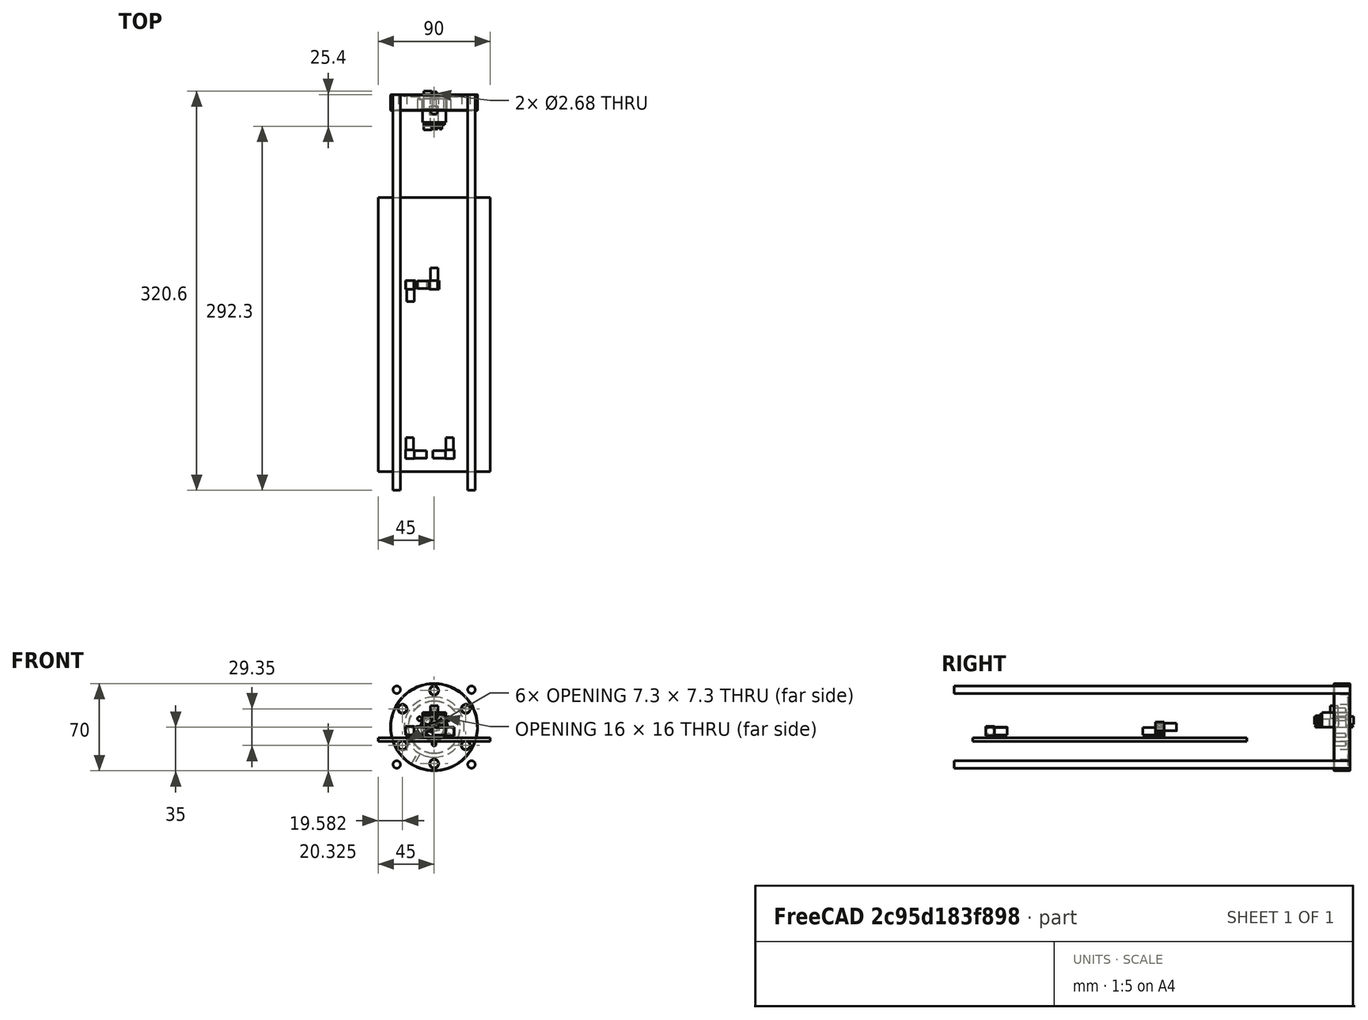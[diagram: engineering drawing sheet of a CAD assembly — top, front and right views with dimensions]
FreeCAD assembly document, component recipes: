
FREECAD ASSEMBLY — COMPONENT RECIPES ("MechanicalCF35Mount_Assembly")

This assembly document has 11 components, labeled P0..P10 below (a component is one placed body or linked part). 6 of them carry a construction recipe — the FreeCAD feature program that regenerates the part from scratch, quoted from this document or its linked companion documents; the rest are supplied as boundary geometry only. No exploded tour is included for this assembly.
COMPONENT P0 — recipe-attached ("Frontplane", a linked part whose construction recipe lives in a companion FreeCAD document of the same project; that document's serialized recipe follows).
Construction recipe (the companion document, serialized — sketch geometry with constraints, then the solid features built on it; lengths are millimeters unless a unit is written):

FCSTD DOCUMENT  (FreeCAD 0.20R29603 (Git))
Label: MechanicalCF35Mount001
License: All rights reserved
LicenseURL: http://en.wikipedia.org/wiki/All_rights_reserved
objects: Part::Feature×20, Part::Cylinder×15, TechDraw::DrawViewDimension×13, Part::Compound×12, TechDraw::DrawProjGroupItem×5, Part::Cut×4, Part::Box×1, Part::Fillet×1, TechDraw::DrawSVGTemplate×1, TechDraw::DrawProjGroup×1, TechDraw::DrawPage×1
note: 53 computed .brp shape members not serialized (recipe doc carries the construction recipe); baked Part::Feature solids carry a one-line shape summary decoded from their .brp

FEATURE [Part::Feature] Solid  label="Hositrad_CFA35-16D"
  shape: bbox 70 x 12.7 x 70 mm, 88 faces (baked)
FEATURE [Part::Feature] _7192_01_CF
  shape: bbox 33.78 x 40.23 x 14.22 mm, 39 faces, 0 solids (baked)
FEATURE [Part::Feature] _7192_01_CF001
  Placement = pos=(0,0,-39.0113) rot=(1,0,0;1.5708rad)
  shape: bbox 14 x 7.506 x 26.34 mm, 46 faces, 0 solids (baked)
FEATURE [Part::Feature] _7192_01_CF002
  Placement = pos=(0,0,-58.2625) rot=(-0.03621,0.706643,0.706643;3.21398rad)
  shape: bbox 18.12 x 10.39 x 7.838 mm, 29 faces, 0 solids (baked)
FEATURE [Part::Feature] _7192_01_CF003
  Placement = pos=(0,0,-42.2965) rot=(0.8891,-0.323652,-0.323652;1.68807rad)
  shape: bbox 16.99 x 16.03 x 5.603 mm, 25 faces, 0 solids (baked)
FEATURE [Part::Feature] _7192_01_CF004
  Placement = pos=(0,0,-35.56) rot=(0,0.707107,-0.707107;3.14159rad)
  shape: bbox 22.78 x 12.72 x 33.85 mm, 35 faces, 0 solids (baked)
FEATURE [Part::Feature] _7192_01_CF005
  Placement = pos=(0,0,-36.7339) rot=(0.997746,-0.047454,-0.047454;1.57305rad)
  shape: bbox 7.007 x 7.007 x 0.8128 mm, 6 faces, 0 solids (baked)
FEATURE [Part::Feature] _7192_01_CF006
  Placement = pos=(0,0,-66.0654) rot=(0.57735,0.57735,0.57735;2.0944rad)
  shape: bbox 2.416 x 2.416 x 39.37 mm, 29 faces, 0 solids (baked)
FEATURE [Part::Feature] _7192_01_CF007
  Placement = pos=(0,0,-32.2253) rot=(0.196732,0.693288,-0.693288;3.5301rad)
  shape: bbox 26.96 x 26.96 x 13.28 mm, 55 faces, 0 solids (baked)
FEATURE [Part::Feature] _7192_01_CF008
  Placement = pos=(0,0,-46.1699) rot=(0.196732,0.693288,-0.693288;3.5301rad)
  shape: bbox 34.28 x 29.27 x 4.775 mm, 16 faces, 0 solids (baked)
FEATURE [Part::Feature] _7192_01_CF009
  Placement = pos=(0,0,-22.86) rot=(0.196732,0.693288,-0.693288;3.5301rad)
  shape: bbox 24.3 x 24.3 x 12.6 mm, 19 faces, 0 solids (baked)
FEATURE [Part::Feature] _7192_01_CF010
  Placement = pos=(0,0,-12.7) rot=(0.196732,0.693288,-0.693288;3.5301rad)
  shape: bbox 26.42 x 26.42 x 12.7 mm, 14 faces, 0 solids (baked)
FEATURE [Part::Feature] _7192_01_CF011
  Placement = pos=(0,0,-42.1821) rot=(0.196732,0.693288,-0.693288;3.5301rad)
  shape: bbox 43.95 x 37.52 x 5.044 mm, 27 faces, 0 solids (baked)
FEATURE [Part::Feature] _7192_01_CF012
  Placement = pos=(0,0,-35.56) rot=(0.079728,0.704856,0.704856;2.98247rad)
  shape: bbox 15.4 x 15.4 x 39.12 mm, 6 faces, 0 solids (baked)
FEATURE [Part::Feature] _7192_01_CF013
  Placement = pos=(0,0,-26.6954) rot=(0.165786,0.697322,0.697322;2.81301rad)
  shape: bbox 5.339 x 4.281 x 34.06 mm, 6 faces, 0 solids (baked)
FEATURE [Part::Feature] _7192_01_CF014
  Placement = pos=(0,0,6.7564) rot=(0.205998,0.691941,-0.691941;3.54791rad)
  shape: bbox 9.907 x 7.446 x 1.311 mm, 4 faces, 0 solids (baked)
FEATURE [Part::Feature] _7192_01_CF015
  Placement = pos=(0,0,-7.9756) rot=(1,0,0;1.5708rad)
  shape: bbox 22.78 x 12.72 x 22.32 mm, 35 faces, 0 solids (baked)
FEATURE [Part::Feature] _7192_01_CF016
  Placement = pos=(0,0,22.3805) rot=(0.205998,0.691941,-0.691941;3.54791rad)
  shape: bbox 3.344 x 3.344 x 15.27 mm, 29 faces, 0 solids (baked)
FEATURE [Part::Feature] _7192_01_CF017
  Placement = pos=(0,0,6.7564) rot=(1,0,0;1.5708rad)
  shape: bbox 10.8 x 10.8 x 1.524 mm, 10 faces, 0 solids (baked)
FEATURE [Part::Compound] Compound  label="CF16BNCFeedthrough"
  Links = -> [_7192_01_CF,_7192_01_CF001,_7192_01_CF002,_7192_01_CF003,_7192_01_CF004,_7192_01_CF005,_7192_01_CF006,_7192_01_CF007,_7192_01_CF008,_7192_01_CF009,_7192_01_CF010,_7192_01_CF011,_7192_01_CF012,_7192_01_CF013,_7192_01_CF014,_7192_01_CF015,_7192_01_CF016,_7192_01_CF017]
  Placement = pos=(0,0,0) rot=(-1,0,0;1.5708rad)
FEATURE [Part::Box] Box  label="Würfel"
  AttacherType = Attacher::AttachEngine3D
  Height = 100
  Length = 100
  Placement = pos=(-50,0,-50) rot=(0,0,1;0rad)
  Width = 12.7
FEATURE [Part::Cylinder] Cylinder  label="Zylinder"
  Angle = 360
  AttacherType = Attacher::AttachEngine3D
  FirstAngle = 0
  Height = 12.7
  Placement = pos=(0,12.7,0) rot=(1,0,0;1.5708rad)
  Radius = 35.5
  SecondAngle = 0
FEATURE [Part::Cut] Cut
  Base = -> Box
  Tool = -> Cylinder
FEATURE [Part::Cylinder] Cylinder001  label="Zylinder001"
  Angle = 360
  AttacherType = Attacher::AttachEngine3D
  FirstAngle = 0
  Height = 100
  Placement = pos=(0,6.35,-50) rot=(0,0,1;0rad)
  Radius = 2.46
  SecondAngle = 0
FEATURE [Part::Cylinder] Cylinder002  label="Zylinder002"
  Angle = 360
  AttacherType = Attacher::AttachEngine3D
  FirstAngle = 0
  Height = 100
  Placement = pos=(0,6.35,-50) rot=(0,0,1;0rad)
  Radius = 2.46
  SecondAngle = 0
FEATURE [Part::Compound] Compound001
  Links = -> [Cylinder002]
  Placement = pos=(0,0,0) rot=(0,1,0;1.5708rad)
FEATURE [Part::Compound] Compound002  label="SetscrewCoreholes"
  Links = -> [Compound001,Cylinder001]
FEATURE [Part::Cut] Cut001
  Base = -> Cut
  Tool = -> Compound002
FEATURE [Part::Cylinder] Cylinder003  label="Zylinder003"
  Angle = 360
  AttacherType = Attacher::AttachEngine3D
  FirstAngle = 0
  Height = 12
  Placement = pos=(-30,6.3,-50) rot=(0,0,1;0rad)
  Radius = 2.46
  SecondAngle = 0
FEATURE [Part::Cylinder] Cylinder004  label="Zylinder004"
  Angle = 360
  AttacherType = Attacher::AttachEngine3D
  FirstAngle = 0
  Height = 12
  Placement = pos=(30,6.3,-50) rot=(0,0,1;0rad)
  Radius = 2.46
  SecondAngle = 0
FEATURE [Part::Compound] Compound003
  Links = -> [Cylinder003,Cylinder004]
FEATURE [Part::Cylinder] Cylinder005  label="Zylinder005"
  Angle = 360
  AttacherType = Attacher::AttachEngine3D
  FirstAngle = 0
  Height = 12
  Placement = pos=(-30,6.3,-50) rot=(0,0,1;0rad)
  Radius = 2.46
  SecondAngle = 0
FEATURE [Part::Cylinder] Cylinder006  label="Zylinder006"
  Angle = 360
  AttacherType = Attacher::AttachEngine3D
  FirstAngle = 0
  Height = 12
  Placement = pos=(30,6.3,-50) rot=(0,0,1;0rad)
  Radius = 2.46
  SecondAngle = 0
FEATURE [Part::Compound] Compound004
  Links = -> [Cylinder005,Cylinder006]
  Placement = pos=(0,0,0) rot=(0,-1,0;1.5708rad)
FEATURE [Part::Cylinder] Cylinder007  label="Zylinder007"
  Angle = 360
  AttacherType = Attacher::AttachEngine3D
  FirstAngle = 0
  Height = 12
  Placement = pos=(-30,6.3,-50) rot=(0,0,1;0rad)
  Radius = 2.46
  SecondAngle = 0
FEATURE [Part::Cylinder] Cylinder008  label="Zylinder008"
  Angle = 360
  AttacherType = Attacher::AttachEngine3D
  FirstAngle = 0
  Height = 12
  Placement = pos=(30,6.3,-50) rot=(0,0,1;0rad)
  Radius = 2.46
  SecondAngle = 0
FEATURE [Part::Compound] Compound005
  Links = -> [Cylinder007,Cylinder008]
  Placement = pos=(0,0,0) rot=(0,1,0;3.14159rad)
FEATURE [Part::Cylinder] Cylinder009  label="Zylinder009"
  Angle = 360
  AttacherType = Attacher::AttachEngine3D
  FirstAngle = 0
  Height = 12
  Placement = pos=(-30,6.3,-50) rot=(0,0,1;0rad)
  Radius = 2.46
  SecondAngle = 0
FEATURE [Part::Cylinder] Cylinder010  label="Zylinder010"
  Angle = 360
  AttacherType = Attacher::AttachEngine3D
  FirstAngle = 0
  Height = 12
  Placement = pos=(30,6.3,-50) rot=(0,0,1;0rad)
  Radius = 2.46
  SecondAngle = 0
FEATURE [Part::Compound] Compound006
  Links = -> [Cylinder009,Cylinder010]
  Placement = pos=(0,0,0) rot=(0,1,0;-4.71239rad)
FEATURE [Part::Compound] Compound007  label="M6Mountscrews"
  Links = -> [Compound003,Compound004,Compound005,Compound006]
FEATURE [Part::Cut] Cut002
  Base = -> Cut001
  Tool = -> Compound007
FEATURE [Part::Cylinder] Cylinder011  label="Zylinder011"
  Angle = 360
  AttacherType = Attacher::AttachEngine3D
  FirstAngle = 0
  Height = 300
  Placement = pos=(30,12.7,30) rot=(1,0,0;1.5708rad)
  Radius = 2.38
  SecondAngle = 0
FEATURE [Part::Cylinder] Cylinder012  label="Zylinder012"
  Angle = 360
  AttacherType = Attacher::AttachEngine3D
  FirstAngle = 0
  Height = 300
  Placement = pos=(30,12.7,30) rot=(1,0,0;1.5708rad)
  Radius = 2.38
  SecondAngle = 0
FEATURE [Part::Compound] Compound008
  Links = -> [Cylinder012]
  Placement = pos=(0,0,0) rot=(0,1,0;1.5708rad)
FEATURE [Part::Cylinder] Cylinder013  label="Zylinder013"
  Angle = 360
  AttacherType = Attacher::AttachEngine3D
  FirstAngle = 0
  Height = 300
  Placement = pos=(30,12.7,30) rot=(1,0,0;1.5708rad)
  Radius = 2.38
  SecondAngle = 0
FEATURE [Part::Compound] Compound009
  Links = -> [Cylinder013]
  Placement = pos=(0,0,0) rot=(0,1,0;3.14159rad)
FEATURE [Part::Cylinder] Cylinder014  label="Zylinder014"
  Angle = 360
  AttacherType = Attacher::AttachEngine3D
  FirstAngle = 0
  Height = 300
  Placement = pos=(30,12.7,30) rot=(1,0,0;1.5708rad)
  Radius = 2.38
  SecondAngle = 0
FEATURE [Part::Compound] Compound010
  Links = -> [Cylinder014]
  Placement = pos=(0,0,0) rot=(0,-1,0;1.5708rad)
FEATURE [Part::Compound] Compound014  label="M6ThreadRods"
  Links = -> [Cylinder011,Compound008,Compound009,Compound010]
FEATURE [Part::Cut] Cut003
  Base = -> Cut002
  Tool = -> Compound014
FEATURE [Part::Fillet] Fillet
  Base = -> Cut003
  Edges = 2 edges r=2: [Edge2,Edge3]
FEATURE [Part::Feature] Fillet_solid  label="Fillet (Solid)"
  shape: bbox 100 x 12.7 x 100 mm, 33 faces (baked)
FEATURE [TechDraw::DrawSVGTemplate] Template
  EditableTexts = Designed_by_Name=Thomas Spielauer; FC-Date=2023-07-05; FC-SC=mm; FC-SH=01; FC-Title=CF40 electronics housing; Subtitle=Front plate
  Height = 210
  Orientation = 1
  Width = 297
FEATURE [TechDraw::DrawProjGroupItem] ProjItem  label="Front"
  CoarseView = false
  Direction = (0,-1,0)
  Focus = 100
  HardHidden = false
  IsoCount = 0
  IsoHidden = false
  IsoVisible = false
  LockPosition = true
  Perspective = false
  Rotation = 0
  RotationVector = (0,0,1)
  ScaleType = 2
  SeamHidden = false
  SeamVisible = true
  SmoothHidden = false
  SmoothVisible = true
  Source = -> [Fillet]
  Type = 0
  X = 0
  XDirection = (0,0,1)
  Y = 0
FEATURE [TechDraw::DrawProjGroupItem] ProjItem001  label="Right"
  CoarseView = false
  Direction = (0,-1e-16,1)
  Focus = 100
  HardHidden = false
  IsoCount = 0
  IsoHidden = false
  IsoVisible = false
  LockPosition = false
  Perspective = false
  Rotation = 0
  RotationVector = (1,0,0)
  ScaleType = 2
  SeamHidden = false
  SeamVisible = true
  SmoothHidden = false
  SmoothVisible = true
  Source = -> [Fillet]
  Type = 2
  X = -67.6611
  XDirection = (0,1,1e-16)
  Y = 0
FEATURE [TechDraw::DrawProjGroupItem] ProjItem002  label="Bottom"
  CoarseView = false
  Direction = (1,0,0)
  Focus = 100
  HardHidden = false
  IsoCount = 0
  IsoHidden = false
  IsoVisible = false
  LockPosition = false
  Perspective = false
  Rotation = 0
  RotationVector = (1,0,0)
  ScaleType = 2
  SeamHidden = false
  SeamVisible = true
  SmoothHidden = false
  SmoothVisible = true
  Source = -> [Fillet]
  Type = 5
  X = 0
  XDirection = (0,0,1)
  Y = 73.816
FEATURE [TechDraw::DrawProjGroupItem] ProjItem003  label="Left"
  CoarseView = false
  Direction = (0,-1e-16,-1)
  Focus = 100
  HardHidden = false
  IsoCount = 0
  IsoHidden = false
  IsoVisible = false
  LockPosition = false
  Perspective = false
  Rotation = 0
  RotationVector = (1,0,0)
  ScaleType = 2
  SeamHidden = false
  SeamVisible = true
  SmoothHidden = false
  SmoothVisible = true
  Source = -> [Fillet]
  Type = 1
  X = 105.155
  XDirection = (0,-1,1e-16)
  Y = 0
FEATURE [TechDraw::DrawProjGroupItem] ProjItem004  label="Top"
  CoarseView = false
  Direction = (-1,0,0)
  Focus = 100
  HardHidden = false
  IsoCount = 0
  IsoHidden = false
  IsoVisible = false
  LockPosition = false
  Perspective = false
  Rotation = 0
  RotationVector = (1,0,0)
  ScaleType = 2
  SeamHidden = false
  SeamVisible = true
  SmoothHidden = false
  SmoothVisible = true
  Source = -> [Fillet]
  Type = 4
  X = 0
  XDirection = (0,0,1)
  Y = -75.3562
FEATURE [TechDraw::DrawProjGroup] ProjGroup
  Anchor = -> ProjItem
  AutoDistribute = true
  LockPosition = false
  ProjectionType = 0
  Rotation = 0
  ScaleType = 0
  Source = -> [Fillet]
  Views = -> [ProjItem,ProjItem001,ProjItem002,ProjItem003,ProjItem004]
  X = 91.0868
  Y = 118.279
  spacingX = 0
  spacingY = 0
FEATURE [TechDraw::DrawViewDimension] Dimension
  AngleOverride = false
  Arbitrary = false
  ArbitraryTolerances = false
  EqualTolerance = true
  ExtensionAngle = 0
  FormatSpec = %.2w
  FormatSpecOverTolerance = %+.2w
  FormatSpecUnderTolerance = %+.2w
  Inverted = false
  LineAngle = 0
  LockPosition = false
  MeasureType = 1
  OverTolerance = 0
  References2D = -> [ProjItem003]
  Rotation = 0
  ScaleType = 0
  TheoreticalExact = false
  Type = 0
  UnderTolerance = 0
  X = 27.7422
  Y = 2.49993
FEATURE [TechDraw::DrawViewDimension] Dimension001
  AngleOverride = false
  Arbitrary = false
  ArbitraryTolerances = false
  EqualTolerance = true
  ExtensionAngle = 0
  FormatSpec = %.2w
  FormatSpecOverTolerance = %+.2w
  FormatSpecUnderTolerance = %+.2w
  Inverted = false
  LineAngle = 0
  LockPosition = false
  MeasureType = 1
  OverTolerance = 0
  References2D = -> [ProjItem004]
  Rotation = 0
  ScaleType = 0
  TheoreticalExact = false
  Type = 0
  UnderTolerance = 0
  X = -0.515822
  Y = -20.0124
FEATURE [TechDraw::DrawViewDimension] Dimension002
  AngleOverride = false
  Arbitrary = false
  ArbitraryTolerances = false
  EqualTolerance = true
  ExtensionAngle = 0
  FormatSpec = ⌀%.2w
  FormatSpecOverTolerance = %+.2w
  FormatSpecUnderTolerance = %+.2w
  Inverted = false
  LineAngle = 0
  LockPosition = false
  MeasureType = 1
  OverTolerance = 0
  References2D = -> [ProjItem]
  Rotation = 0
  ScaleType = 0
  TheoreticalExact = false
  Type = 5
  UnderTolerance = 0
  X = 0.325472
  Y = 8.03302
FEATURE [TechDraw::DrawViewDimension] Dimension003
  AngleOverride = false
  Arbitrary = false
  ArbitraryTolerances = false
  EqualTolerance = true
  ExtensionAngle = 0
  FormatSpec = ⌀%.2w (M6 4x)
  FormatSpecOverTolerance = %+.2w
  FormatSpecUnderTolerance = %+.2w
  Inverted = false
  LineAngle = 0
  LockPosition = false
  MeasureType = 1
  OverTolerance = 0
  References2D = -> [ProjItem]
  Rotation = 0
  ScaleType = 0
  TheoreticalExact = false
  Type = 5
  UnderTolerance = 0
  X = -23.9583
  Y = 40.0197
FEATURE [TechDraw::DrawViewDimension] Dimension004
  AngleOverride = false
  Arbitrary = false
  ArbitraryTolerances = false
  EqualTolerance = true
  ExtensionAngle = 0
  FormatSpec = %.2w
  FormatSpecOverTolerance = %+.2w
  FormatSpecUnderTolerance = %+.2w
  Inverted = false
  LineAngle = 0
  LockPosition = false
  MeasureType = 1
  OverTolerance = 0
  References2D = -> [ProjItem]
  Rotation = 0
  ScaleType = 0
  TheoreticalExact = false
  Type = 0
  UnderTolerance = 0
  X = 39.4213
  Y = 67.0173
FEATURE [TechDraw::DrawViewDimension] Dimension005
  AngleOverride = false
  Arbitrary = false
  ArbitraryTolerances = false
  EqualTolerance = true
  ExtensionAngle = 0
  FormatSpec = %.2w
  FormatSpecOverTolerance = %+.2w
  FormatSpecUnderTolerance = %+.2w
  Inverted = false
  LineAngle = 0
  LockPosition = false
  MeasureType = 1
  OverTolerance = 0
  References2D = -> [ProjItem]
  Rotation = 0
  ScaleType = 0
  TheoreticalExact = false
  Type = 0
  UnderTolerance = 0
  X = 34.38
  Y = 42.4999
FEATURE [TechDraw::DrawViewDimension] Dimension006
  AngleOverride = false
  Arbitrary = false
  ArbitraryTolerances = false
  EqualTolerance = true
  ExtensionAngle = 0
  FormatSpec = %.2w
  FormatSpecOverTolerance = %+.2w
  FormatSpecUnderTolerance = %+.2w
  Inverted = false
  LineAngle = 0
  LockPosition = false
  MeasureType = 1
  OverTolerance = 0
  References2D = -> [ProjItem]
  Rotation = 0
  ScaleType = 0
  TheoreticalExact = false
  Type = 0
  UnderTolerance = 0
  X = 71.4033
  Y = -19.5166
FEATURE [TechDraw::DrawViewDimension] Dimension007
  AngleOverride = false
  Arbitrary = false
  ArbitraryTolerances = false
  EqualTolerance = true
  ExtensionAngle = 0
  FormatSpec = %.2w
  FormatSpecOverTolerance = %+.2w
  FormatSpecUnderTolerance = %+.2w
  Inverted = false
  LineAngle = 0
  LockPosition = false
  MeasureType = 1
  OverTolerance = 0
  References2D = -> [ProjItem]
  Rotation = 0
  ScaleType = 0
  TheoreticalExact = false
  Type = 0
  UnderTolerance = 0
  X = -1.26969
  Y = 60.8859
FEATURE [TechDraw::DrawViewDimension] Dimension008
  AngleOverride = false
  Arbitrary = false
  ArbitraryTolerances = false
  EqualTolerance = true
  ExtensionAngle = 0
  FormatSpec = ⌀%.2w (M6 3x pro Seite)
  FormatSpecOverTolerance = %+.2w
  FormatSpecUnderTolerance = %+.2w
  Inverted = false
  LineAngle = 0
  LockPosition = false
  MeasureType = 1
  OverTolerance = 0
  References2D = -> [ProjItem003]
  Rotation = 0
  ScaleType = 0
  TheoreticalExact = false
  Type = 5
  UnderTolerance = 0
  X = 55.193
  Y = 36.5443
FEATURE [TechDraw::DrawViewDimension] Dimension009
  AngleOverride = false
  Arbitrary = false
  ArbitraryTolerances = false
  EqualTolerance = true
  ExtensionAngle = 0
  FormatSpec = %.2w
  FormatSpecOverTolerance = %+.2w
  FormatSpecUnderTolerance = %+.2w
  Inverted = false
  LineAngle = 0
  LockPosition = false
  MeasureType = 1
  OverTolerance = 0
  References2D = -> [ProjItem003]
  Rotation = 0
  ScaleType = 0
  TheoreticalExact = false
  Type = 0
  UnderTolerance = 0
  X = -14.0854
  Y = 64.8143
FEATURE [TechDraw::DrawViewDimension] Dimension010
  AngleOverride = false
  Arbitrary = false
  ArbitraryTolerances = false
  EqualTolerance = true
  ExtensionAngle = 0
  FormatSpec = %.2w
  FormatSpecOverTolerance = %+.2w
  FormatSpecUnderTolerance = %+.2w
  Inverted = false
  LineAngle = 0
  LockPosition = false
  MeasureType = 1
  OverTolerance = 0
  References2D = -> [ProjItem003]
  Rotation = 0
  ScaleType = 0
  TheoreticalExact = false
  Type = 0
  UnderTolerance = 0
  X = -20.8153
  Y = 17.1561
FEATURE [TechDraw::DrawViewDimension] Dimension011
  AngleOverride = false
  Arbitrary = false
  ArbitraryTolerances = false
  EqualTolerance = true
  ExtensionAngle = 0
  FormatSpec = %.2w
  FormatSpecOverTolerance = %+.2w
  FormatSpecUnderTolerance = %+.2w
  Inverted = false
  LineAngle = 0
  LockPosition = false
  MeasureType = 1
  OverTolerance = 0
  References2D = -> [ProjItem003]
  Rotation = 0
  ScaleType = 0
  TheoreticalExact = false
  Type = 0
  UnderTolerance = 0
  X = -20.7966
  Y = -12.5001
FEATURE [TechDraw::DrawViewDimension] Dimension012
  AngleOverride = false
  Arbitrary = false
  ArbitraryTolerances = false
  EqualTolerance = true
  ExtensionAngle = 0
  FormatSpec = %.2w
  FormatSpecOverTolerance = %+.2w
  FormatSpecUnderTolerance = %+.2w
  Inverted = false
  LineAngle = 0
  LockPosition = false
  MeasureType = 1
  OverTolerance = 0
  References2D = -> [ProjItem003]
  Rotation = 0
  ScaleType = 0
  TheoreticalExact = false
  Type = 0
  UnderTolerance = 0
  X = 15.28
  Y = -53.2031
FEATURE [TechDraw::DrawPage] Page
  KeepUpdated = true
  NextBalloonIndex = 1
  ProjectionType = 0
  Template = -> Template
  Views = -> [ProjGroup,Dimension,Dimension001,Dimension002,Dimension003,Dimension004,Dimension005,Dimension006,Dimension007,Dimension008,Dimension009,Dimension010,Dimension011,Dimension012]
COMPONENT P1 — geometry summary ("Backplane"; no construction recipe available for this part):
  bounding box: 100.0 x 100.0 x 4.0 mm
  tessellated surface: 3,356 triangles
  volume: 39570 mm^3 (99% of its bounding box)
  symmetry: 2-fold rotationally symmetric about the y axis; 2-fold rotationally symmetric about the z axis; mirror-symmetric across its x mid-plane, z mid-plane
COMPONENT P2 — geometry summary ("Coversheet"; no construction recipe available for this part):
  bounding box: 317.7 x 105.4 x 103.6 mm
  tessellated surface: 6,192 triangles
  volume: 177131 mm^3 (5% of its bounding box)
  symmetry: 2-fold rotationally symmetric about the z axis; mirror-symmetric across its x mid-plane, y mid-plane
COMPONENT P3 — recipe-attached ("Bottomplane", a linked part whose construction recipe lives in a companion FreeCAD document of the same project; that document's serialized recipe follows).
Construction recipe (the companion document, serialized — sketch geometry with constraints, then the solid features built on it; lengths are millimeters unless a unit is written):

FCSTD DOCUMENT  (FreeCAD 0.20R29603 (Git))
Label: MechanicalCF35Mount004
License: All rights reserved
LicenseURL: http://en.wikipedia.org/wiki/All_rights_reserved
objects: Part::Cylinder×14, Part::Compound×10, TechDraw::DrawViewDimension×8, TechDraw::DrawProjGroupItem×2, Part::Box×1, Part::Cut×1, Part::Feature×1, TechDraw::DrawSVGTemplate×1, TechDraw::DrawProjGroup×1, TechDraw::DrawPage×1
note: 27 computed .brp shape members not serialized (recipe doc carries the construction recipe); baked Part::Feature solids carry a one-line shape summary decoded from their .brp

FEATURE [Part::Box] Box  label="Würfel"
  AttacherType = Attacher::AttachEngine3D
  Height = 1.8
  Length = 100
  Placement = pos=(-50,-305,50) rot=(0,0,1;0rad)
  Width = 317.7
FEATURE [Part::Cylinder] Cylinder  label="Zylinder"
  Angle = 360
  AttacherType = Attacher::AttachEngine3D
  FirstAngle = 0
  Height = 20
  Placement = pos=(30,2,40) rot=(0,0,1;0rad)
  Radius = 1.2
  SecondAngle = 0
FEATURE [Part::Cylinder] Cylinder015  label="Zylinder015"
  Angle = 360
  AttacherType = Attacher::AttachEngine3D
  FirstAngle = 0
  Height = 20
  Placement = pos=(-30,2,40) rot=(0,0,1;0rad)
  Radius = 1.2
  SecondAngle = 0
FEATURE [Part::Compound] Compound
  Links = -> [Cylinder,Cylinder015]
FEATURE [Part::Cylinder] Cylinder016  label="Zylinder016"
  Angle = 360
  AttacherType = Attacher::AttachEngine3D
  FirstAngle = 0
  Height = 20
  Placement = pos=(30,2,40) rot=(0,0,1;0rad)
  Radius = 1.2
  SecondAngle = 0
FEATURE [Part::Cylinder] Cylinder017  label="Zylinder017"
  Angle = 360
  AttacherType = Attacher::AttachEngine3D
  FirstAngle = 0
  Height = 20
  Placement = pos=(-30,2,40) rot=(0,0,1;0rad)
  Radius = 1.2
  SecondAngle = 0
FEATURE [Part::Compound] Compound015
  Links = -> [Cylinder016,Cylinder017]
  Placement = pos=(0,0,0) rot=(0,1,0;1.5708rad)
FEATURE [Part::Cylinder] Cylinder018  label="Zylinder018"
  Angle = 360
  AttacherType = Attacher::AttachEngine3D
  FirstAngle = 0
  Height = 20
  Placement = pos=(30,2,40) rot=(0,0,1;0rad)
  Radius = 1.2
  SecondAngle = 0
FEATURE [Part::Cylinder] Cylinder019  label="Zylinder019"
  Angle = 360
  AttacherType = Attacher::AttachEngine3D
  FirstAngle = 0
  Height = 20
  Placement = pos=(-30,2,40) rot=(0,0,1;0rad)
  Radius = 1.2
  SecondAngle = 0
FEATURE [Part::Compound] Compound016
  Links = -> [Cylinder018,Cylinder019]
  Placement = pos=(0,0,0) rot=(0,1,0;3.14159rad)
FEATURE [Part::Cylinder] Cylinder020  label="Zylinder020"
  Angle = 360
  AttacherType = Attacher::AttachEngine3D
  FirstAngle = 0
  Height = 20
  Placement = pos=(30,2,40) rot=(0,0,1;0rad)
  Radius = 1.2
  SecondAngle = 0
FEATURE [Part::Cylinder] Cylinder021  label="Zylinder021"
  Angle = 360
  AttacherType = Attacher::AttachEngine3D
  FirstAngle = 0
  Height = 20
  Placement = pos=(-30,2,40) rot=(0,0,1;0rad)
  Radius = 1.2
  SecondAngle = 0
FEATURE [Part::Compound] Compound017
  Links = -> [Cylinder020,Cylinder021]
  Placement = pos=(0,0,0) rot=(0,-1,0;1.5708rad)
FEATURE [Part::Compound] Compound018  label="M2Corehole"
  Links = -> [Compound017,Compound,Compound015,Compound016]
  Placement = pos=(0,-302,0) rot=(0,0,1;0rad)
FEATURE [Part::Cylinder] Cylinder004  label="Zylinder004"
  Angle = 360
  AttacherType = Attacher::AttachEngine3D
  FirstAngle = 0
  Height = 200
  Placement = pos=(30,6.35,-100) rot=(0,0,1;0rad)
  Radius = 3.3
  SecondAngle = 0
FEATURE [Part::Cylinder] Cylinder005  label="Zylinder005"
  Angle = 360
  AttacherType = Attacher::AttachEngine3D
  FirstAngle = 0
  Height = 200
  Placement = pos=(-30,6.35,-100) rot=(0,0,1;0rad)
  Radius = 3.3
  SecondAngle = 0
FEATURE [Part::Cylinder] Cylinder006  label="Zylinder006"
  Angle = 360
  AttacherType = Attacher::AttachEngine3D
  FirstAngle = 0
  Height = 200
  Placement = pos=(-30,6.35,-100) rot=(0,0,1;0rad)
  Radius = 3.3
  SecondAngle = 0
FEATURE [Part::Cylinder] Cylinder007  label="Zylinder007"
  Angle = 360
  AttacherType = Attacher::AttachEngine3D
  FirstAngle = 0
  Height = 200
  Placement = pos=(30,6.35,-100) rot=(0,0,1;0rad)
  Radius = 3.3
  SecondAngle = 0
FEATURE [Part::Compound] Compound004
  Links = -> [Cylinder006,Cylinder007]
  Placement = pos=(0,0,0) rot=(0,1,0;1.5708rad)
FEATURE [Part::Compound] Compound005
  Links = -> [Cylinder004,Cylinder005,Compound004]
FEATURE [Part::Cylinder] Cylinder008  label="Zylinder008"
  Angle = 360
  AttacherType = Attacher::AttachEngine3D
  FirstAngle = 0
  Height = 200
  Placement = pos=(0,6.35,-100) rot=(0,0,1;0rad)
  Radius = 3.3
  SecondAngle = 0
FEATURE [Part::Cylinder] Cylinder009  label="Zylinder009"
  Angle = 360
  AttacherType = Attacher::AttachEngine3D
  FirstAngle = 0
  Height = 200
  Placement = pos=(0,6.35,-100) rot=(0,0,1;0rad)
  Radius = 3.3
  SecondAngle = 0
FEATURE [Part::Compound] Compound007
  Links = -> [Cylinder009]
  Placement = pos=(0,0,0) rot=(0,1,0;1.5708rad)
FEATURE [Part::Compound] Compound008
  Links = -> [Compound005,Cylinder008,Compound007]
FEATURE [Part::Compound] Compound019
  Links = -> [Compound018,Compound008]
FEATURE [Part::Cut] Cut
  Base = -> Box
  Tool = -> Compound019
FEATURE [Part::Feature] Cut_solid  label="Cut (Solid)"
  shape: bbox 100 x 317.7 x 1.8 mm, 11 faces (baked)
FEATURE [TechDraw::DrawSVGTemplate] Template
  EditableTexts = Designed_by_Name=Thoams Spielauer; FC-Date=2023-07-05; FC-SC=mm; FC-SH=01; FC-Title=CF40 electronics housing; Subtitle=Bottom sheet
  Height = 210
  Orientation = 1
  Width = 297
FEATURE [TechDraw::DrawProjGroupItem] ProjItem  label="Front"
  CoarseView = false
  Direction = (0,0,1)
  Focus = 100
  HardHidden = false
  IsoCount = 0
  IsoHidden = false
  IsoVisible = false
  LockPosition = true
  Perspective = false
  Rotation = 0
  RotationVector = (1,0,0)
  Scale = 0.333333
  ScaleType = 2
  SeamHidden = false
  SeamVisible = true
  SmoothHidden = false
  SmoothVisible = true
  Source = -> [Cut_solid]
  Type = 0
  X = 0
  XDirection = (1,0,0)
  Y = 0
FEATURE [TechDraw::DrawProjGroupItem] ProjItem001  label="Left"
  CoarseView = false
  Direction = (-1,0,1e-16)
  Focus = 100
  HardHidden = false
  IsoCount = 0
  IsoHidden = false
  IsoVisible = false
  LockPosition = false
  Perspective = false
  Rotation = 0
  RotationVector = (1,0,0)
  ScaleType = 2
  SeamHidden = false
  SeamVisible = true
  SmoothHidden = false
  SmoothVisible = true
  Source = -> [Cut_solid]
  Type = 1
  X = 48.3333
  XDirection = (1e-16,0,1)
  Y = 0
FEATURE [TechDraw::DrawProjGroup] ProjGroup
  Anchor = -> ProjItem
  AutoDistribute = true
  LockPosition = false
  ProjectionType = 0
  Rotation = 0
  Scale = 0.333333
  ScaleType = 2
  Source = -> [Cut_solid]
  Views = -> [ProjItem,ProjItem001]
  X = 87.4123
  Y = 128.335
  spacingX = 15
  spacingY = 15
FEATURE [TechDraw::DrawViewDimension] Dimension
  AngleOverride = false
  Arbitrary = false
  ArbitraryTolerances = false
  EqualTolerance = true
  ExtensionAngle = 0
  FormatSpec = %.2w
  FormatSpecOverTolerance = %+.2w
  FormatSpecUnderTolerance = %+.2w
  Inverted = false
  LineAngle = 0
  LockPosition = false
  MeasureType = 1
  OverTolerance = 0
  References2D = -> [ProjItem]
  Rotation = 0
  ScaleType = 0
  TheoreticalExact = false
  Type = 0
  UnderTolerance = 0
  X = -33.2555
  Y = 1.26203
FEATURE [TechDraw::DrawViewDimension] Dimension001
  AngleOverride = false
  Arbitrary = false
  ArbitraryTolerances = false
  EqualTolerance = true
  ExtensionAngle = 0
  FormatSpec = %.2w
  FormatSpecOverTolerance = %+.2w
  FormatSpecUnderTolerance = %+.2w
  Inverted = false
  LineAngle = 0
  LockPosition = false
  MeasureType = 1
  OverTolerance = 0
  References2D = -> [ProjItem]
  Rotation = 0
  ScaleType = 0
  TheoreticalExact = false
  Type = 0
  UnderTolerance = 0
  X = -1.23797
  Y = -66.7912
FEATURE [TechDraw::DrawViewDimension] Dimension002
  AngleOverride = false
  Arbitrary = false
  ArbitraryTolerances = false
  EqualTolerance = true
  ExtensionAngle = 0
  FormatSpec = %.2w
  FormatSpecOverTolerance = %+.2w
  FormatSpecUnderTolerance = %+.2w
  Inverted = false
  LineAngle = 0
  LockPosition = false
  MeasureType = 1
  OverTolerance = 0
  References2D = -> [ProjItem001]
  Rotation = 0
  ScaleType = 0
  TheoreticalExact = false
  Type = 0
  UnderTolerance = 0
  X = 0.102835
  Y = 63.4252
FEATURE [TechDraw::DrawViewDimension] Dimension003
  AngleOverride = false
  Arbitrary = false
  ArbitraryTolerances = false
  EqualTolerance = true
  ExtensionAngle = 0
  FormatSpec = %.2w
  FormatSpecOverTolerance = %+.2w
  FormatSpecUnderTolerance = %+.2w
  Inverted = false
  LineAngle = 0
  LockPosition = false
  MeasureType = 1
  OverTolerance = 0
  References2D = -> [ProjItem]
  Rotation = 0
  ScaleType = 0
  TheoreticalExact = false
  Type = 0
  UnderTolerance = 0
  X = 7.70254
  Y = 64.3208
FEATURE [TechDraw::DrawViewDimension] Dimension004
  AngleOverride = false
  Arbitrary = false
  ArbitraryTolerances = false
  EqualTolerance = true
  ExtensionAngle = 0
  FormatSpec = %.2w
  FormatSpecOverTolerance = %+.2w
  FormatSpecUnderTolerance = %+.2w
  Inverted = false
  LineAngle = 0
  LockPosition = false
  MeasureType = 1
  OverTolerance = 0
  References2D = -> [ProjItem]
  Rotation = 0
  ScaleType = 0
  TheoreticalExact = false
  Type = 0
  UnderTolerance = 0
  X = -12.2736
  Y = 64.3062
FEATURE [TechDraw::DrawViewDimension] Dimension005
  AngleOverride = false
  Arbitrary = false
  ArbitraryTolerances = false
  EqualTolerance = true
  ExtensionAngle = 0
  FormatSpec = ⌀%.2w (3x)
  FormatSpecOverTolerance = %+.2w
  FormatSpecUnderTolerance = %+.2w
  Inverted = false
  LineAngle = 0
  LockPosition = false
  MeasureType = 1
  OverTolerance = 0
  References2D = -> [ProjItem]
  Rotation = 0
  ScaleType = 0
  TheoreticalExact = false
  Type = 5
  UnderTolerance = 0
  X = 1.44604
  Y = 36.618
FEATURE [TechDraw::DrawViewDimension] Dimension006
  AngleOverride = false
  Arbitrary = false
  ArbitraryTolerances = false
  EqualTolerance = true
  ExtensionAngle = 0
  FormatSpec = %.2w
  FormatSpecOverTolerance = %+.2w
  FormatSpecUnderTolerance = %+.2w
  Inverted = false
  LineAngle = 0
  LockPosition = false
  MeasureType = 1
  OverTolerance = 0
  References2D = -> [ProjItem]
  Rotation = 0
  ScaleType = 0
  TheoreticalExact = false
  Type = 0
  UnderTolerance = 0
  X = 12.0421
  Y = -78.1672
FEATURE [TechDraw::DrawViewDimension] Dimension007
  AngleOverride = false
  Arbitrary = false
  ArbitraryTolerances = false
  EqualTolerance = true
  ExtensionAngle = 0
  FormatSpec = ⌀%.2w (2x)
  FormatSpecOverTolerance = %+.2w
  FormatSpecUnderTolerance = %+.2w
  Inverted = false
  LineAngle = 0
  LockPosition = false
  MeasureType = 1
  OverTolerance = 0
  References2D = -> [ProjItem]
  Rotation = 0
  ScaleType = 0
  TheoreticalExact = false
  Type = 5
  UnderTolerance = 0
  X = -9.25376
  Y = -35.5101
FEATURE [TechDraw::DrawPage] Page
  KeepUpdated = true
  NextBalloonIndex = 1
  ProjectionType = 0
  Template = -> Template
  Views = -> [ProjGroup,Dimension,Dimension001,Dimension002,Dimension003,Dimension004,Dimension005,Dimension006,Dimension007]
COMPONENT P4 — geometry summary ("Fusion (Solid)001"; no construction recipe available for this part):
  bounding box: 17.0 x 17.0 x 7.0 mm
  tessellated surface: 1,524 triangles
  volume: 908 mm^3 (45% of its bounding box)
  symmetry: mirror-symmetric across its x mid-plane
COMPONENT P5 — geometry summary ("Preamp002"; no construction recipe available for this part):
  bounding box: 31.2 x 18.8 x 11.6 mm
  tessellated surface: 2,114 triangles
  volume: 4867 mm^3 (71% of its bounding box)
COMPONENT P6 — geometry summary ("Preamp003"; no construction recipe available for this part):
  bounding box: 31.2 x 18.8 x 11.6 mm
  tessellated surface: 2,114 triangles
  volume: 4867 mm^3 (71% of its bounding box)
COMPONENT P7 — recipe-attached ("Common (Solid)", a linked part whose construction recipe lives in a companion FreeCAD document of the same project; that document's serialized recipe follows).
Construction recipe (the companion document, serialized — sketch geometry with constraints, then the solid features built on it; lengths are millimeters unless a unit is written):

FCSTD DOCUMENT  (FreeCAD 0.20R29603 (Git))
Label: MechanicalCF35Mount005
License: All rights reserved
LicenseURL: http://en.wikipedia.org/wiki/All_rights_reserved
objects: Part::Cylinder×6, Part::Compound×5, Part::Box×2, Part::Cut×2, Part::MultiCommon×1, Part::Feature×1
note: 17 computed .brp shape members not serialized (recipe doc carries the construction recipe); baked Part::Feature solids carry a one-line shape summary decoded from their .brp

FEATURE [Part::Cylinder] Cylinder  label="Zylinder"
  Angle = 360
  AttacherType = Attacher::AttachEngine3D
  FirstAngle = 0
  Height = 317.7
  Placement = pos=(-30,12.7,-30) rot=(1,0,0;1.5708rad)
  Radius = 3
  SecondAngle = 0
FEATURE [Part::Cylinder] Cylinder001  label="Zylinder001"
  Angle = 360
  AttacherType = Attacher::AttachEngine3D
  FirstAngle = 0
  Height = 317.7
  Placement = pos=(-30,12.7,-30) rot=(1,0,0;1.5708rad)
  Radius = 3
  SecondAngle = 0
FEATURE [Part::Compound] Compound
  Links = -> [Cylinder001]
  Placement = pos=(0,0,0) rot=(0,1,0;1.5708rad)
FEATURE [Part::Cylinder] Cylinder002  label="Zylinder002"
  Angle = 360
  AttacherType = Attacher::AttachEngine3D
  FirstAngle = 0
  Height = 317.7
  Placement = pos=(-30,12.7,-30) rot=(1,0,0;1.5708rad)
  Radius = 3
  SecondAngle = 0
FEATURE [Part::Compound] Compound001
  Links = -> [Cylinder002]
  Placement = pos=(0,0,0) rot=(0,1,0;3.14159rad)
FEATURE [Part::Cylinder] Cylinder003  label="Zylinder003"
  Angle = 360
  AttacherType = Attacher::AttachEngine3D
  FirstAngle = 0
  Height = 317.7
  Placement = pos=(-30,12.7,-30) rot=(1,0,0;1.5708rad)
  Radius = 3
  SecondAngle = 0
FEATURE [Part::Compound] Compound002
  Links = -> [Cylinder003]
  Placement = pos=(0,0,0) rot=(0,-1,0;1.5708rad)
FEATURE [Part::Compound] Compound003  label="ThreadedRodsM6"
  Links = -> [Compound002,Compound,Compound001,Cylinder]
  Placement = pos=(0,20,0) rot=(0,0,1;0rad)
FEATURE [Part::Box] Box  label="Würfel"
  AttacherType = Attacher::AttachEngine3D
  Height = 2.8
  Length = 90
  Placement = pos=(-45,-10,-11.5) rot=(0,0,1;0rad)
  Width = 220
FEATURE [Part::Box] Box001  label="Würfel001"
  AttacherType = Attacher::AttachEngine3D
  Height = 100
  Length = 100
  Placement = pos=(-50,0,-50) rot=(0,0,1;0rad)
  Width = 2.5
FEATURE [Part::Compound] Compound004
  Links = -> [Compound003,Box]
FEATURE [Part::Cut] Cut
  Base = -> Box001
  Tool = -> Compound004
FEATURE [Part::Cylinder] Cylinder004  label="Zylinder004"
  Angle = 360
  AttacherType = Attacher::AttachEngine3D
  FirstAngle = 0
  Height = 10
  Placement = pos=(0,6,0) rot=(1,0,0;1.5708rad)
  Radius = 37
  SecondAngle = 0
FEATURE [Part::Cut] Cut001
  Base = -> Cut
  Tool = -> Cylinder004
FEATURE [Part::Cylinder] Cylinder005  label="Zylinder005"
  Angle = 360
  AttacherType = Attacher::AttachEngine3D
  FirstAngle = 0
  Height = 10
  Placement = pos=(0,6,0) rot=(1,0,0;1.5708rad)
  Radius = 50
  SecondAngle = 0
FEATURE [Part::MultiCommon] Common
  Shapes = -> [Cut001,Cylinder005]
FEATURE [Part::Feature] Common_solid  label="Common (Solid)"
  shape: bbox 100 x 2.5 x 100 mm, 19 faces (baked)
COMPONENT P8 — same part as P7; its construction recipe is shown at P7.
COMPONENT P9 — same part as P7; its construction recipe is shown at P7.
COMPONENT P10 — same part as P7; its construction recipe is shown at P7.
PROVENANCE & LICENSES
A FreeCAD (.FCStd) document from a public repository crawl; recipes are the document's own serialized feature recipes (and, for linked parts, companion documents' recipes).
License: bsd.
